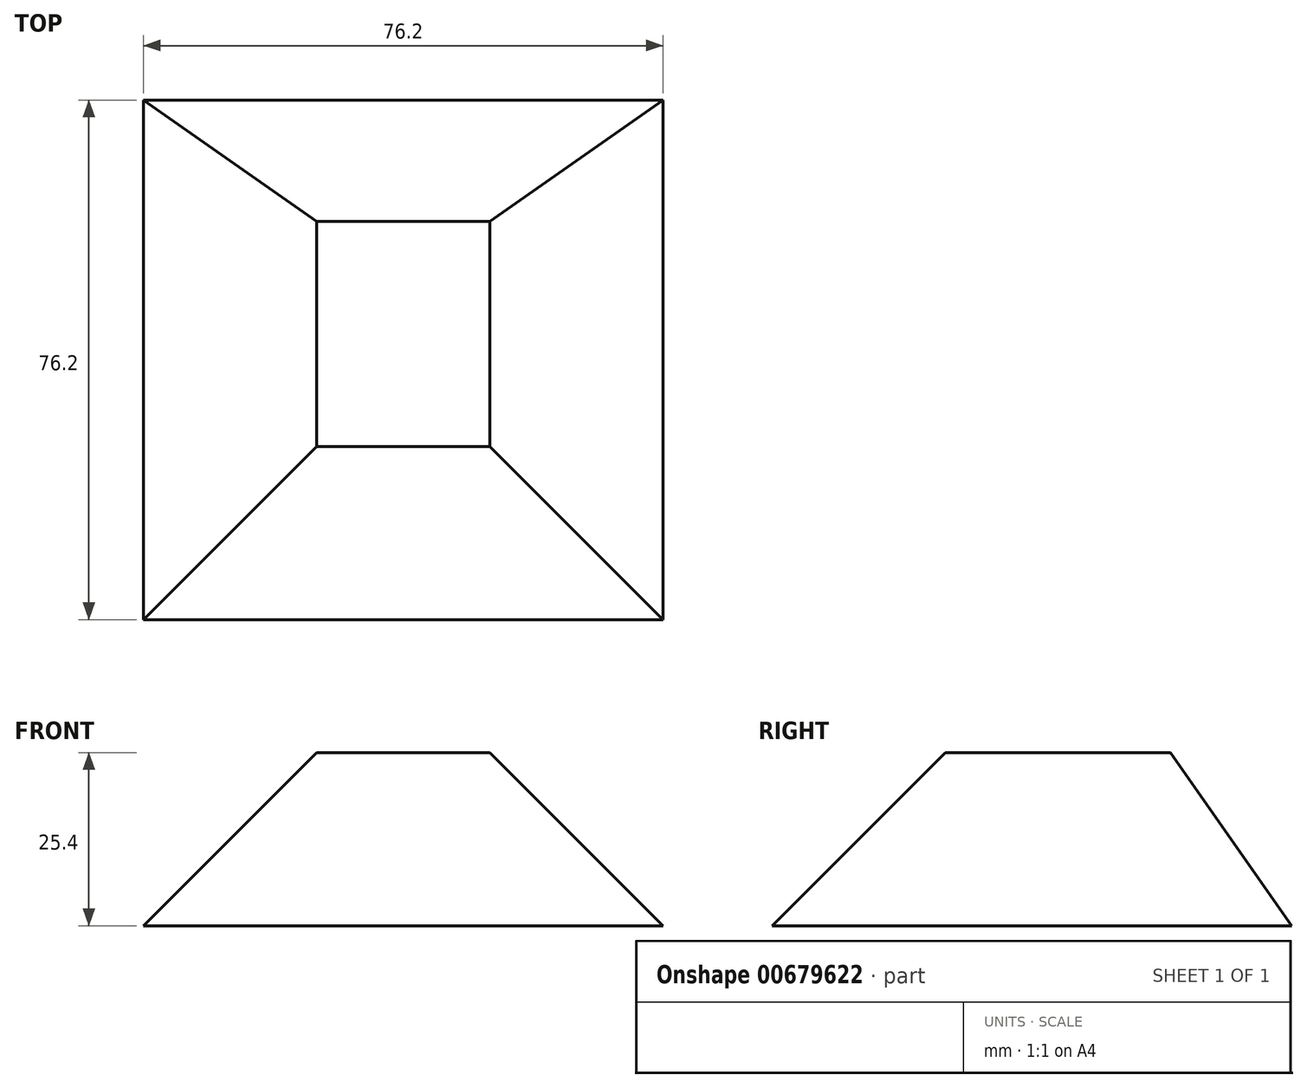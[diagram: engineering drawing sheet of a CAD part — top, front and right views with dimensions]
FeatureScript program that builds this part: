
annotation { "Feature Type Name" : "Feature", "Feature Type Description" : "" }
export const myFeature = defineFeature(function(context is Context, id is Id, definition is map)
    precondition{}
    {
        {
            var Q0;
            Q0=qCreatedBy(makeId("Top.planeOp"),FACE);
            var sketch = newSketch(context, id + "F0", { "sketchPlane" : qUnion([Q0])});
            skLineSegment(sketch, "E0.bottom", {"start": v(-43.21, 34.67) * mm, "end": v(32.99, 34.67) * mm});
            skLineSegment(sketch, "E0.top", {"start": v(-43.21, -41.53) * mm, "end": v(32.99, -41.53) * mm});
            skLineSegment(sketch, "E0.left", {"start": v(-43.21, 34.67) * mm, "end": v(-43.21, -41.53) * mm});
            skLineSegment(sketch, "E0.right", {"start": v(32.99, 34.67) * mm, "end": v(32.99, -41.53) * mm});
            skSolve(sketch);
        }
        {
            var Q0;
            Q0=makeQuery(id+"F0.imprint","IMPRINT",FACE,{"disambiguationData":[TD([[makeQuery(id+"F0.imprint","IMPRINT",EDGE,{"derivedFrom":sQuery(id+"F0.wireOp",EDGE,"E0.bottom")}),-1.0]])]});
            extrude(context, id + "F1", {"entities" : qUnion([Q0]), "depth" : 25.4 * mm, "offsetDistance" : 25.4 * mm});
        }
        {
            var Q0;
            Q0=makeQuery(id+"F1.opExtrude","CAP_EDGE",EDGE,{"disambiguationData":[OSD([sQuery(id+"F0.wireOp",EDGE,"E0.right")])],"isStart":false});
            chamfer(context, id + "F2", {"entities" : qUnion([Q0]), "chamferType" : ChamferType.OFFSET_ANGLE, "width" : 25.4 * mm, "oppositeDirection" : false, "angle" : 45 * degree, "tangentPropagation" : true});
        }
        {
            var Q0;
            Q0=makeQuery(id+"F1.opExtrude","CAP_EDGE",EDGE,{"disambiguationData":[OSD([sQuery(id+"F0.wireOp",EDGE,"E0.bottom")])],"isStart":false});
            chamfer(context, id + "F3", {"entities" : qUnion([Q0]), "chamferType" : ChamferType.OFFSET_ANGLE, "width" : 25.4 * mm, "oppositeDirection" : false, "angle" : 35 * degree, "tangentPropagation" : true});
        }
        {
            var Q0;
            Q0=makeQuery(id+"F1.opExtrude","CAP_EDGE",EDGE,{"disambiguationData":[OSD([sQuery(id+"F0.wireOp",EDGE,"E0.left")])],"isStart":false});
            chamfer(context, id + "F4", {"entities" : qUnion([Q0]), "chamferType" : ChamferType.OFFSET_ANGLE, "width" : 25.4 * mm, "oppositeDirection" : false, "angle" : 45 * degree, "tangentPropagation" : true});
        }
        {
            var Q0;
            Q0=makeQuery(id+"F1.opExtrude","CAP_EDGE",EDGE,{"disambiguationData":[OSD([sQuery(id+"F0.wireOp",EDGE,"E0.top")])],"isStart":false});
            chamfer(context, id + "F5", {"entities" : qUnion([Q0]), "chamferType" : ChamferType.OFFSET_ANGLE, "width" : 25.4 * mm, "oppositeDirection" : false, "angle" : 45 * degree, "tangentPropagation" : true});
        }
    });
